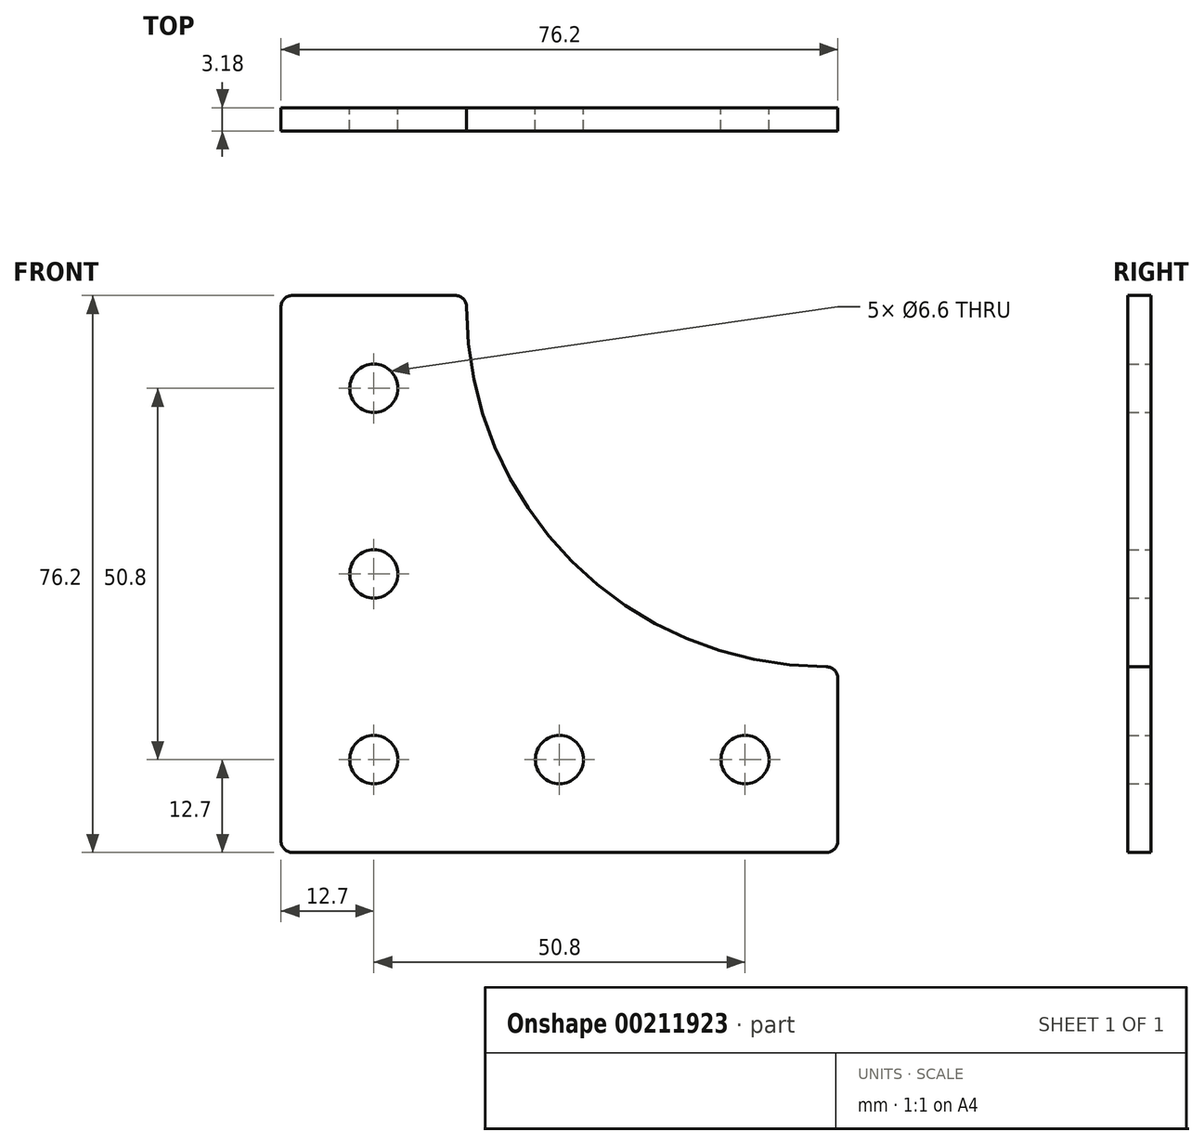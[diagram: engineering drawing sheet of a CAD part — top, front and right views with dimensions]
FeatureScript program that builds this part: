
annotation { "Feature Type Name" : "Feature", "Feature Type Description" : "" }
export const myFeature = defineFeature(function(context is Context, id is Id, definition is map)
    precondition{}
    {
        {
            var Q0;
            Q0=qCreatedBy(makeId("Front.planeOp"),FACE);
            var sketch = newSketch(context, id + "F0", { "sketchPlane" : qUnion([Q0])});
            skLineSegment(sketch, "E0.bottom", {"start": v(-23.81, 50.8) * mm, "end": v(-1.59, 50.8) * mm});
            skLineSegment(sketch, "E0.top", {"start": v(-23.81, -25.4) * mm, "end": v(0, -25.4) * mm});
            skLineSegment(sketch, "E0.left", {"start": v(-25.4, 49.21) * mm, "end": v(-25.4, -23.81) * mm});
            skLineSegment(sketch, "E1.bottom", {"start": v(0, -25.4) * mm, "end": v(49.21, -25.4) * mm});
            skLineSegment(sketch, "E1.right", {"start": v(50.8, -23.81) * mm, "end": v(50.8, -1.59) * mm});
            skCircle(sketch, "E2", {"center": v(-12.7, -12.7) * mm, "radius": 3.3 * mm});
            skCircle(sketch, "E3", {"center": v(-12.7, 12.7) * mm, "radius": 3.3 * mm});
            skCircle(sketch, "E4", {"center": v(-12.7, 38.1) * mm, "radius": 3.3 * mm});
            skCircle(sketch, "E5", {"center": v(12.7, -12.7) * mm, "radius": 3.3 * mm});
            skCircle(sketch, "E6", {"center": v(38.1, -12.7) * mm, "radius": 3.3 * mm});
            skPoint(sketch, "E7.visualSharp", {"position": v(-25.4, 50.8) * mm});
            skPoint(sketch, "E8.visualSharp", {"position": v(0, 50.8) * mm});
            skPoint(sketch, "E9.visualSharp", {"position": v(0, 0) * mm});
            skPoint(sketch, "E10.visualSharp", {"position": v(50.8, 0) * mm});
            skArc(sketch, "E10.filletArc", {"start": v(50.8, -1.59) * mm, "mid": v(50.34, -0.46) * mm, "end": v(49.21, 0) * mm});
            skPoint(sketch, "E11.visualSharp", {"position": v(50.8, -25.4) * mm});
            skArc(sketch, "E11.filletArc", {"start": v(49.21, -25.4) * mm, "mid": v(50.34, -24.94) * mm, "end": v(50.8, -23.81) * mm});
            skPoint(sketch, "E12.visualSharp", {"position": v(-25.4, -25.4) * mm});
            skArc(sketch, "E12.filletArc", {"start": v(-25.4, -23.81) * mm, "mid": v(-24.94, -24.94) * mm, "end": v(-23.81, -25.4) * mm});
            skArc(sketch, "E13.filletArc", {"start": v(-23.81, 50.8) * mm, "mid": v(-24.94, 50.34) * mm, "end": v(-25.4, 49.21) * mm});
            skArc(sketch, "E14.filletArc", {"start": v(0, 49.21) * mm, "mid": v(-0.46, 50.34) * mm, "end": v(-1.59, 50.8) * mm});
            skArc(sketch, "E15", {"start": v(0, 49.21) * mm, "mid": v(14.41, 14.41) * mm, "end": v(49.21, 0) * mm});
            skSolve(sketch);
        }
        {
            var Q0;
            Q0 = qSketchRegion(id + "F0", true);
            extrude(context, id + "F1", {"entities" : qUnion([Q0]), "depth" : 3.17 * mm});
        }
    });
